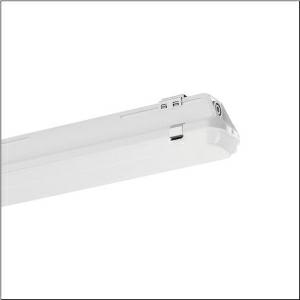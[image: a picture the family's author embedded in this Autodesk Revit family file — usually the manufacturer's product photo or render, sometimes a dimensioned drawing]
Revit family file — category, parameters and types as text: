
# Revit family: monsun_r__12_51fp10mp4b0q_003c
name_source: partatom
category: Lighting Fixtures
units: mm (PartAtom-declared; Revit-internal decimal feet)

## family parameters
Cut with Voids When Loaded = No
Host = Face
Light Source = No
Part Type = Normal
Room Calculation Point = No
Round Connector Dimension = Use Diameter
Shared = No

## types (1)
- --- (1 x LED, 12070 lm, 66.2 W, 4000K)
    Apparent Load = 66 VA
    CIE Flux Codes = 47 76 93 94 100
    Color Rendering = 80
    Color Temperature = 4000K
    Default Elevation = 1800 mm
    Description = Monsun® 12, damp-proof luminaire, chain hanger, primary optical cover: enclosure, of PMMA, light emission: direct distribution, primary light characteristic: symmetric, installation type: suspended mounting, surface-mounted, horizontal mounting, vertical mounting, LED rated luminous flux: 12.070 lm, light colour: 840, colour temperature: 4000K, control gear: ECG, with terminal, 3-pole, max. 2.5mm², mains connection: 220..240V, AC, 50/60Hz, rated input power: 66W, luminaire housing, of glass-fibre reinforced polyester, uncoated, bright grey, length: 1.590 mm, width: 90 mm, height: 88mm, clip for enclosure, of stainless steel (V2A), ceiling mounting element, of stainless steel (V2A), chain hanger, of stainless steel (V2A), protection rating (complete): IP66, insulation class (complete): insulation class I (protective earthing), certification: CE, ENEC, VDE, protection symbol: D, impact resistance: IK04, permissible ambient temperature for indoor applications: -35..+35°C, standard: EN 50419, EN 60598-2-1, no direct snow, no direct sun, no direct rain, for indoor or canopied outdoor use, corresponds to IFS (International Featured Standards) requirements for safety and quality in the food industry, for animal farming (ammonia tested): for use in cowhouse, pig house, horse-stables... (not for use in poultry stables), AT max for animal farming = 40°C, packaging unit: 1 piece
    Height = 89 mm
    Lamp = 1 x LED
    Lamp Light Flux = 12070 lm
    Lamp Power = 66.2 W
    Lamp count = 1
    Length = 1590 mm
    Luminous efficacy = 182 lm/W
    Manufacturer = Siteco
    ModVariant = No
    Model = 51FP10MP4B0Q
    Mounting Place = Ceiling
    Mounting Type = Pendant
    Number of Poles = 1
    OnlyDefault = Yes
    Power Factor = 1
    Product Name = Monsun® 12
    Product group = damp-proof luminaire | ceiling pendant
    ProductGroupID = 908
    Protection Class = Protection class I
    Protection Degree = IP 66
    RLX_Detail_Level = 1
    RlxData = <blob elided: 89869 chars, md5=ac5acc7c>
    Socket = socket
    Standby Power = 0 W
    System Light Flux = 12070 lm
    System Power = 66 W
    Type Comments = factory setting: luminous flux: 100 % | (A | C | E) | 155 mA
    Type Image = l_1004748.jpg
    URL = http://relux.com
    VarID = @adj_136079
    Voltage = 0 V
    Weight = 0.00 kg
    Width = 90 mm

## geometry (parser evidence)
native form markers: Blend x4, Sweep x15
no freeform markers — native parametric forms only
